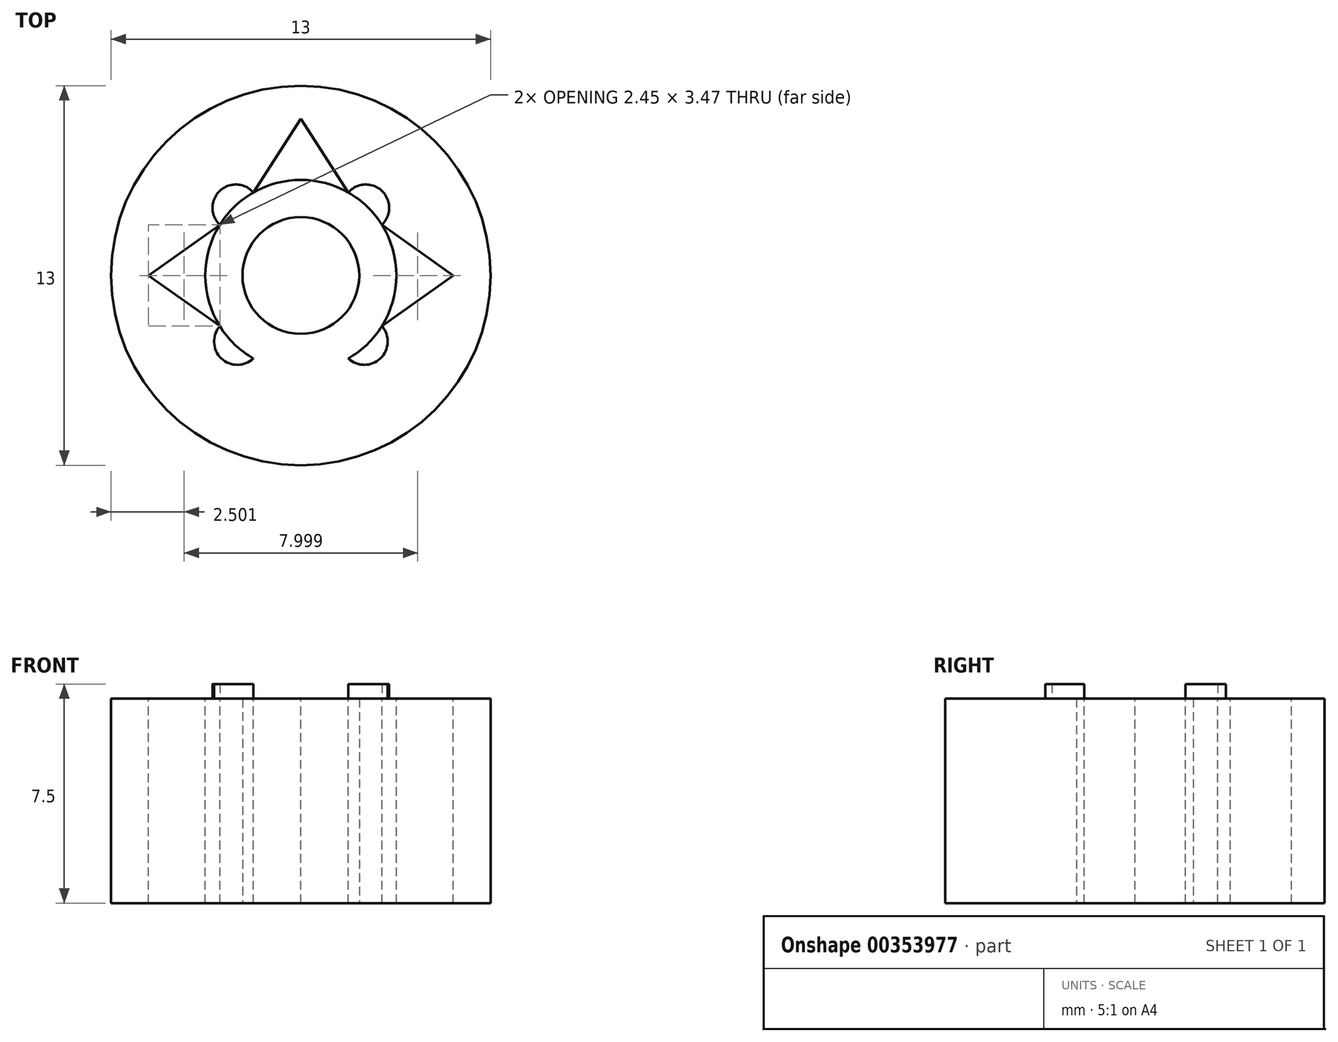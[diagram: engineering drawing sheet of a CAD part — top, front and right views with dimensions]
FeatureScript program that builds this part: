
annotation { "Feature Type Name" : "Feature", "Feature Type Description" : "" }
export const myFeature = defineFeature(function(context is Context, id is Id, definition is map)
    precondition{}
    {
        {
            var Q0;
            Q0=qCreatedBy(makeId("Top.planeOp"),FACE);
            var sketch = newSketch(context, id + "F0", { "sketchPlane" : qUnion([Q0])});
            skCircle(sketch, "E0", {"center": v(0, 0) * mm, "radius": 6.5 * mm});
            skCircle(sketch, "E1", {"center": v(0, 0) * mm, "radius": 2 * mm});
            skPoint(sketch, "E2.right.end.orphan", {"position": v(-2.92, 0) * mm});
            skPoint(sketch, "E3.bottom.start.orphan", {"position": v(3.79, 0) * mm});
            skSolve(sketch);
        }
        {
            var Q0;
            Q0=makeQuery(id+"F0.imprint","IMPRINT",FACE,{"disambiguationData":[TD([[makeQuery(id+"F0.imprint","IMPRINT",EDGE,{"derivedFrom":sQuery(id+"F0.wireOp",EDGE,"E0")}),1.0]])]});
            extrude(context, id + "F1", {"entities" : qUnion([Q0]), "depth" : 7 * mm});
        }
        {
            var Q0;
            Q0=makeQuery(id+"F1.opExtrude","CAP_FACE",FACE,{"disambiguationData":[OSD([sQuery(id+"F0.wireOp",EDGE,"E0"),sQuery(id+"F0.wireOp",EDGE,"E1")])],"isStart":false});
            var sketch = newSketch(context, id + "F2", { "sketchPlane" : qUnion([Q0])});
            skCircle(sketch, "E4", {"center": v(0, 0) * mm, "radius": 3.27 * mm});
            skLineSegment(sketch, "E5", {"start": v(-1.62, 2.84) * mm, "end": v(0, 5.37) * mm});
            skLineSegment(sketch, "E6", {"start": v(0, 5.37) * mm, "end": v(1.62, 2.84) * mm});
            skLineSegment(sketch, "E7", {"start": v(-1.62, -2.84) * mm, "end": v(0, -5.37) * mm});
            skLineSegment(sketch, "E8", {"start": v(0, -5.37) * mm, "end": v(1.62, -2.84) * mm});
            skLineSegment(sketch, "E9", {"start": v(-2.78, 1.74) * mm, "end": v(-5.22, 0) * mm});
            skLineSegment(sketch, "E10", {"start": v(-5.22, 0) * mm, "end": v(-2.78, -1.74) * mm});
            skLineSegment(sketch, "E11", {"start": v(2.78, 1.74) * mm, "end": v(5.22, 0) * mm});
            skLineSegment(sketch, "E12", {"start": v(5.22, 0) * mm, "end": v(2.78, -1.74) * mm});
            skArc(sketch, "E13", {"start": v(-1.62, 2.84) * mm, "mid": v(-2.78, 2.9) * mm, "end": v(-2.78, 1.74) * mm});
            skArc(sketch, "E14", {"start": v(2.78, 1.74) * mm, "mid": v(2.78, 2.9) * mm, "end": v(1.62, 2.84) * mm});
            skArc(sketch, "E15", {"start": v(1.62, -2.84) * mm, "mid": v(2.73, -2.84) * mm, "end": v(2.78, -1.74) * mm});
            skArc(sketch, "E16", {"start": v(-2.78, -1.74) * mm, "mid": v(-2.73, -2.84) * mm, "end": v(-1.62, -2.84) * mm});
            skSolve(sketch);
        }
        {
            var Q0;
            {var subQ0=sQuery(id+"F2.wireOp",EDGE,"E9");Q0=makeQuery(id+"F2.imprint","IMPRINT",FACE,{"disambiguationData":[TD([[makeQuery(id+"F2.imprint","IMPRINT",EDGE,{"derivedFrom":subQ0}),1.0]])]});}
            var Q1;
            {var subQ0=sQuery(id+"F2.wireOp",EDGE,"E7");Q1=makeQuery(id+"F2.imprint","IMPRINT",FACE,{"disambiguationData":[TD([[makeQuery(id+"F2.imprint","IMPRINT",EDGE,{"derivedFrom":subQ0}),1.0]])]});}
            var Q2;
            {var subQ0=sQuery(id+"F2.wireOp",EDGE,"E11");Q2=makeQuery(id+"F2.imprint","IMPRINT",FACE,{"disambiguationData":[TD([[makeQuery(id+"F2.imprint","IMPRINT",EDGE,{"derivedFrom":subQ0}),-1.0]])]});}
            var Q3;
            {var subQ0=sQuery(id+"F2.wireOp",EDGE,"E5");Q3=makeQuery(id+"F2.imprint","IMPRINT",FACE,{"disambiguationData":[TD([[makeQuery(id+"F2.imprint","IMPRINT",EDGE,{"derivedFrom":subQ0}),-1.0]])]});}
            extrude(context, id + "F3", {"entities" : qUnion([Q0, Q1, Q2, Q3]), "operationType" : NewBodyOperationType.REMOVE, "oppositeDirection" : true, "depth" : 25 * mm});
        }
        {
            var Q0;
            {var subQ0=sQuery(id+"F2.wireOp",EDGE,"E14");Q0=makeQuery(id+"F2.imprint","IMPRINT",FACE,{"disambiguationData":[TD([[makeQuery(id+"F2.imprint","IMPRINT",EDGE,{"derivedFrom":subQ0}),1.0]])]});}
            var Q1;
            {var subQ0=sQuery(id+"F2.wireOp",EDGE,"E13");Q1=makeQuery(id+"F2.imprint","IMPRINT",FACE,{"disambiguationData":[TD([[makeQuery(id+"F2.imprint","IMPRINT",EDGE,{"derivedFrom":subQ0}),1.0]])]});}
            var Q2;
            {var subQ0=sQuery(id+"F2.wireOp",EDGE,"E16");Q2=makeQuery(id+"F2.imprint","IMPRINT",FACE,{"disambiguationData":[TD([[makeQuery(id+"F2.imprint","IMPRINT",EDGE,{"derivedFrom":subQ0}),1.0]])]});}
            var Q3;
            {var subQ0=sQuery(id+"F2.wireOp",EDGE,"E15");Q3=makeQuery(id+"F2.imprint","IMPRINT",FACE,{"disambiguationData":[TD([[makeQuery(id+"F2.imprint","IMPRINT",EDGE,{"derivedFrom":subQ0}),1.0]])]});}
            extrude(context, id + "F4", {"entities" : qUnion([Q0, Q1, Q2, Q3]), "operationType" : NewBodyOperationType.ADD, "depth" : 0.5 * mm});
        }
    });
